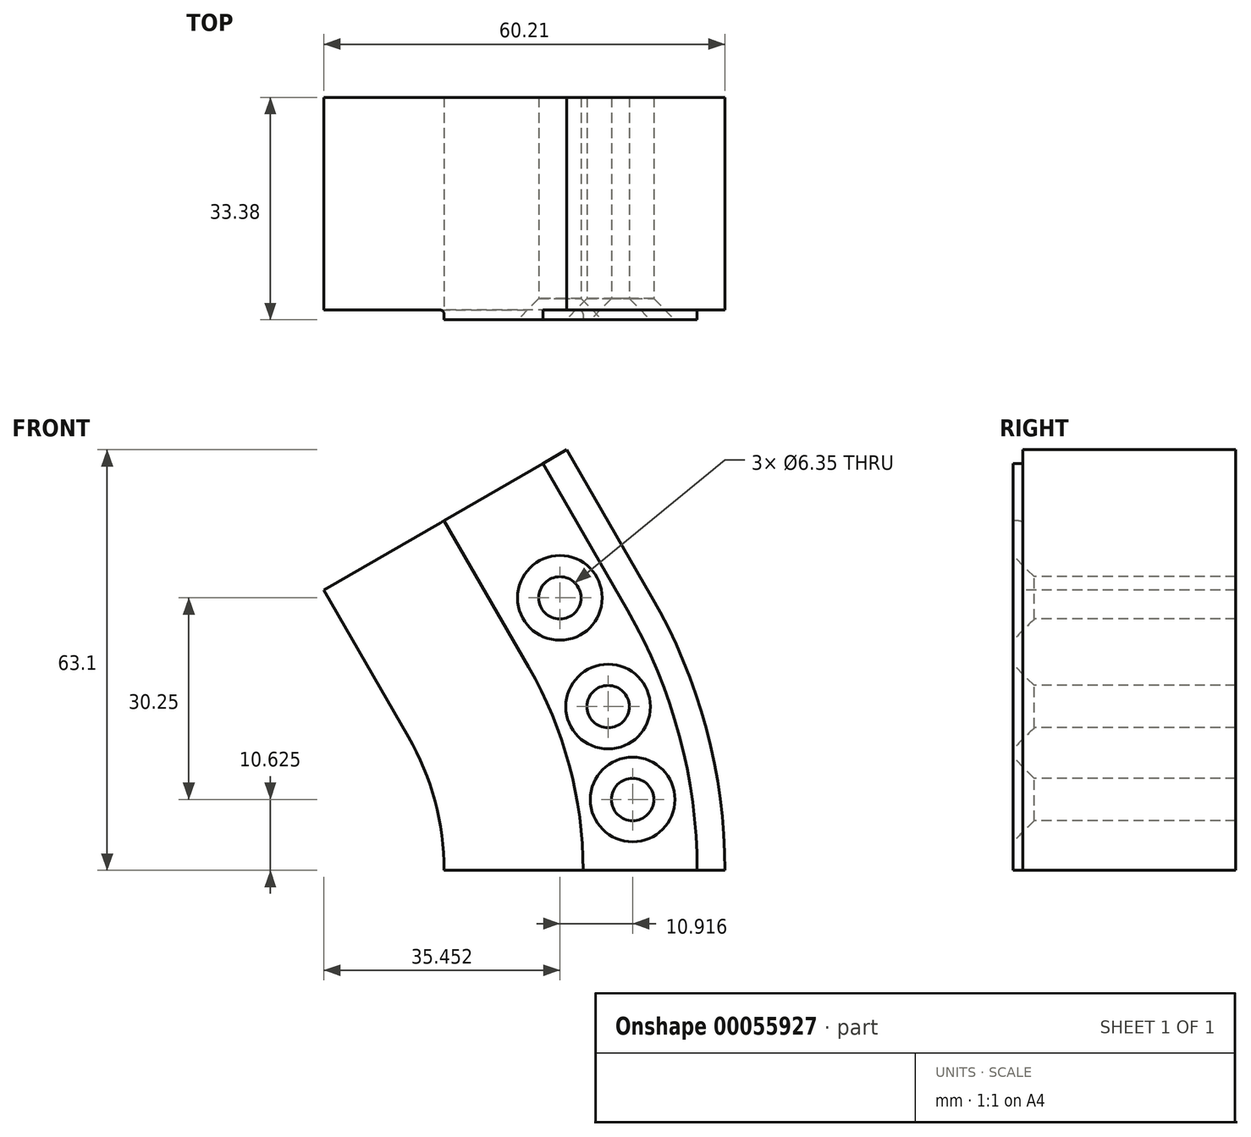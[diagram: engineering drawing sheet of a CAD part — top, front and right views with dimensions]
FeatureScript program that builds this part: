
annotation { "Feature Type Name" : "Feature", "Feature Type Description" : "" }
export const myFeature = defineFeature(function(context is Context, id is Id, definition is map)
    precondition{}
    {
        {
            var Q0;
            Q0=qCreatedBy(makeId("Top.planeOp"),FACE);
            var sketch = newSketch(context, id + "F0", { "sketchPlane" : qUnion([Q0])});
            skLineSegment(sketch, "E0.rect.bottom", {"start": v(21.07, 15.96) * mm, "end": v(-21.07, 15.96) * mm});
            skLineSegment(sketch, "E0.rect.top", {"start": v(21.07, -15.96) * mm, "end": v(16.9, -15.96) * mm});
            skLineSegment(sketch, "E0.rect.left", {"start": v(21.07, 15.96) * mm, "end": v(21.07, -15.96) * mm});
            skLineSegment(sketch, "E0.rect.right", {"start": v(-21.07, 15.96) * mm, "end": v(-21.07, -15.96) * mm});
            skPoint(sketch, "E0.rect.middle", {"position": v(0, 0) * mm});
            skLineSegment(sketch, "E1.rect.top", {"start": v(16.9, -17.42) * mm, "end": v(-0.2, -17.42) * mm});
            skLineSegment(sketch, "E1.rect.left", {"start": v(16.9, -15.96) * mm, "end": v(16.9, -17.42) * mm});
            skLineSegment(sketch, "E1.rect.right", {"start": v(-0.2, -15.96) * mm, "end": v(-0.2, -17.42) * mm});
            skPoint(sketch, "E1.rect.middle", {"position": v(8.35, -3.86) * mm});
            skPoint(sketch, "E1.rect.bottom.end.orphan", {"position": v(-0.2, 9.7) * mm});
            skPoint(sketch, "E2.orphan", {"position": v(16.9, 9.7) * mm});
            skLineSegment(sketch, "E3.trimOffspring", {"start": v(-0.2, -15.96) * mm, "end": v(-21.07, -15.96) * mm});
            skSolve(sketch);
        }
        {
            var Q0;
            Q0=qCreatedBy(makeId("Top.planeOp"),FACE);
            var sketch = newSketch(context, id + "F1", { "sketchPlane" : qUnion([Q0])});
            skLineSegment(sketch, "E4", {"start": v(-61.13, 31.82) * mm, "end": v(-61.13, -28.48) * mm});
            skSolve(sketch);
        }
        {
            var Q0;
            Q0 = qSketchRegion(id + "F0", true);
            var Q1;
            Q1=sQuery(id+"F1.wireOp",EDGE,"E4");
            revolve(context, id + "F2", {"entities" : qUnion([Q0]), "axis" : qUnion([Q1]), "revolveType" : RevolveType.ONE_DIRECTION, "angle" : 30 * degree});
        }
        {
            var Q0;
            Q0=makeQuery(id+"F2.opRevolve","CAP_FACE",FACE,{"disambiguationData":[OSD([sQuery(id+"F0.wireOp",EDGE,"E0.rect.bottom"),sQuery(id+"F0.wireOp",EDGE,"E0.rect.top"),sQuery(id+"F0.wireOp",EDGE,"E0.rect.left"),sQuery(id+"F0.wireOp",EDGE,"E0.rect.right"),sQuery(id+"F0.wireOp",EDGE,"E1.rect.top"),sQuery(id+"F0.wireOp",EDGE,"E1.rect.left"),sQuery(id+"F0.wireOp",EDGE,"E1.rect.right"),sQuery(id+"F0.wireOp",EDGE,"E3.trimOffspring")])],"isStart":false});
            extrude(context, id + "F3", {"entities" : qUnion([Q0]), "operationType" : NewBodyOperationType.ADD, "depth" : 25.4 * mm});
        }
        {
            var Q0;
            Q0=makeQuery(id+"F2.opRevolve","SWEPT_EDGE",EDGE,{"disambiguationData":[OSD([sQuery(id+"F0.wireOp",EDGE,"E1.rect.right"),sQuery(id+"F0.wireOp",EDGE,"E3.trimOffspring")])]});
            var Q1;
            Q1=makeQuery(id+"F3.opExtrude","SWEPT_EDGE",EDGE,{"disambiguationData":[OSD([sQuery(id+"F0.wireOp",EDGE,"E1.rect.right"),sQuery(id+"F0.wireOp",EDGE,"E3.trimOffspring")])]});
            fillet(context, id + "F4", {"entities" : qUnion([Q0, Q1]), "radius" : 0.64 * mm, "tangentPropagation" : true, "allowEdgeOverflow" : false});
        }
        {
            var Q0;
            {var subQ0=sQuery(id+"F0.wireOp",EDGE,"E1.rect.top");Q0=makeQuery(id+"F3.boolean.opBoolean","MERGE",FACE,{"derivedFrom":[makeQuery(id+"F2.opRevolve","SWEPT_FACE",FACE,{"disambiguationData":[OSD([subQ0])]}),makeQuery(id+"F3.opExtrude","SWEPT_FACE",FACE,{"disambiguationData":[OSD([subQ0])]})]});}
            var sketch = newSketch(context, id + "F5", { "sketchPlane" : qUnion([Q0])});
            skCircle(sketch, "E5", {"center": v(7.23, 10.63) * mm, "radius": 3.63 * mm});
            skCircle(sketch, "E6", {"center": v(3.55, 24.56) * mm, "radius": 6.17 * mm});
            skCircle(sketch, "E7", {"center": v(-3.69, 40.88) * mm, "radius": 4.73 * mm});
            skSolve(sketch);
        }
        {
            var Q0;
            Q0=sQuery(id+"F5.wireOp",VERTEX,"E5.center");
            var Q1;
            Q1=sQuery(id+"F5.wireOp",VERTEX,"E6.center");
            var Q2;
            Q2=sQuery(id+"F5.wireOp",VERTEX,"E7.center");
            var Q3;
            Q3=makeQuery(id+"F2.opRevolve","SWEPT_BODY",BODY,{"disambiguationData":[OSD([sQuery(id+"F0.wireOp",EDGE,"E0.rect.bottom"),sQuery(id+"F0.wireOp",EDGE,"E0.rect.top"),sQuery(id+"F0.wireOp",EDGE,"E0.rect.left"),sQuery(id+"F0.wireOp",EDGE,"E0.rect.right"),sQuery(id+"F0.wireOp",EDGE,"E1.rect.top"),sQuery(id+"F0.wireOp",EDGE,"E1.rect.left"),sQuery(id+"F0.wireOp",EDGE,"E1.rect.right"),sQuery(id+"F0.wireOp",EDGE,"E3.trimOffspring")])]});
            hole(context, id + "F6", {"style" : HoleStyle.C_SINK, "holeDiameter" : 6.35 * mm, "cSinkDiameter" : 12.7 * mm, "endStyle" : HoleEndStyle.THROUGH, "locations" : qUnion([Q0, Q1, Q2]), "scope" : qUnion([Q3]), "cSinkAngle" : 90 * degree});
        }
    });
